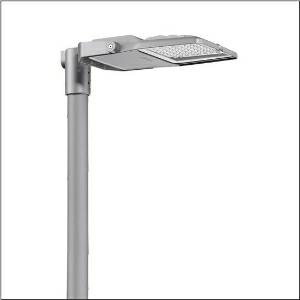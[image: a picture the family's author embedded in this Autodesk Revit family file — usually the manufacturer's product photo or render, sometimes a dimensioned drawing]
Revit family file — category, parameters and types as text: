
# Revit family: floodlight_fl_21_mini___pl61_5xa7776c2c3a_9e20
name_source: partatom
category: Lighting Fixtures
units: mm (PartAtom-declared; Revit-internal decimal feet)

## family parameters
Cut with Voids When Loaded = No
Host = Face
Light Source = No
Part Type = Normal
Room Calculation Point = No
Round Connector Dimension = Use Diameter
Shared = No

## types (1)
- --- (1 x LED, 11960 lm, 89 W, 3000K)
    Apparent Load = 89 VA
    CIE Flux Codes = 33 65 98 100 100
    Color Rendering = 70
    Color Temperature = 3000K
    Default Elevation = 1800 mm
    Description = Floodlight FL 21 mini, floodlight, primary light control with lens, of PMMA, primary optical cover: protective disc, of toughened safety glass, transparent, light distribution: PL61, light emission: direct distribution, installation type: surface-mounted, LED, High Power LED, rated luminous flux: 11.960lm, luminous efficacy: 134lm/W, light colour: 730, colour temperature: 3000K, control gear: Smart Interface (Zhaga), control: flexible luminous flux parameterisation, time-dependent luminous flux control, constant luminous flux control, overheat protection, pre-setting: logarithmic dimming characteristic, with terminal, 6-pole, mains connection: 220..240V, AC, 50/60Hz, start of lifetime: 89W, end of service life: 94W, reduction: 43W, luminaire housing, of diecast aluminium, powder-coated, Siteco® metallic grey (DB 702S), corrosivity category C5 mid according to DIN EN ISO 12944, suitable for swimming pools, chlorine-resistant, sealing non-destructively replaceable, please order mast flange separately, mast bracket, of steel, galvanised, powder-coated, Siteco® metallic grey (DB 702S), Smart Interface below and above, protection rating (complete): IP66, insulation class (complete): insulation class II (safety insulation), certification: CE, ENEC, VDE, protection symbol: D, impact resistance: IK08, permissible operating ambient temperature: -40..+40°C, permissible operating ambient temperature for outdoor applications: -40..+50°C, standard: DIN EN 12944, LABS conformity tested according to VDMA 24364:2018-05, packaging unit: 1 piece

Light Distribution: PL61
    Height = 70 mm
    Lamp = 1 x LED
    Lamp Light Flux = 11960 lm
    Lamp Power = 89 W
    Lamp count = 1
    Length = 485 mm
    Luminous efficacy = 134 lm/W
    Manufacturer = Siteco
    ModVariant = No
    Model = 5XA7776C2C3A
    Number of Poles = 1
    OnlyDefault = Yes
    Power Factor = 1
    Product Name = Floodlight FL 21 mini | PL61
    Product group = floodlight | pylon annexe
    ProductGroupID = 6200
    Protection Class = Protection class II
    Protection Degree = IP 66
    RLX_Detail_Level = 1
    RLX_Emergency_Light_Flux = 0 lm
    RLX_Emergency_Type = 0
    RLX_Emergency_Type_DB = No
    RlxData = <blob elided: 100993 chars, md5=c5fc6d5c>
    Socket = socket
    Standby Power = 0 W
    System Light Flux = 11960 lm
    System Power = 89 W
    Type Comments = factory setting: luminous flux: 100 % | dim-lin: 254 | 456 mA
    Type Image = l_1007125.jpg
    URL = http://relux.com
    VarID = @adj_171998
    Voltage = 0 V
    Weight = 0.00 kg
    Width = 337 mm

## geometry (parser evidence)
native form markers: Blend x4, Sweep x12
no freeform markers — native parametric forms only
